# Revit family: Hager-Volta-IP30-Hollow_wall-empty-NoHosted-CH-en
name_source: partatom
category: Electrical Equipment
units: mm (PartAtom-declared; Revit-internal decimal feet)

## family parameters
Always vertical = Yes
Cut with Voids When Loaded = No
Panel Configuration = Two Columns, Circuits Across
Part Type = Panelboard
Room Calculation Point = No
Round Connector Dimension = Use Diameter
Shared = No
Work Plane-Based = Yes

## types (5) — shared parameters
Default Elevation = 1219 mm
EF000003 - Mounting method = EV000128 - Hollow wall
EF000007 - Colour = EV000202 - White
EF000008 - Width = 330 mm
EF000049 - Depth = 94 mm  [stored 0.308399 ft]
EF000116 - RAL-number = 9010
EF000118 - With mounting plate = No
EF000218 - Built-in depth = 90 mm  [stored 0.295276 ft]
EF000846 - Built-in width = 314 mm  [stored 1.03018 ft]
EF001062 - EMC-version = Yes
EF001088 - Extension possible = Yes
EF001131 - Internal depth = 92 mm
EF001134 - DIN-rail = No
EF001596 - Material housing = EV000139 - Plastic
EF002950 - Width in number of modular spacings = 12
EF006244 - Transparent cover/door = No
EF006306 - With lock = No
EF009212 - Cover model = EV000116 - Closed
EF015776 - Earthing terminal block = No
EF015777 - Neutral terminal block = No
EF015941 - Signal passing door = No
HG000002 - With door or cover = No
HG000003 - Range = Volta
HG000005 - Thickness = 3 mm  [stored 0.00984252 ft]
HG000006 - Flush mounted = Yes
HG000009 - Double swing door = No
HG000010 - Asymmetric doors = No
HG000011 - Empty rows from bottom = No
HG000017 - Distance between poles = 18 mm  [stored 0.0590551 ft]
Manufacturer = Hager
Type Comments = Volta
zero-valued in all types: HG000001 - Number of columns, HG000007 - Number of empty columns, HG000008 - Number of empty rows

## per-type parameters (varying)
| type | EF000040 - Height | EF000266 - Number of rows | EF000332 - Built-in height | HG000004 - Manufacturer reference | Model |
| Recessed mounted  W330 H355 D94.5 12 Modular spacings - VH12NK | 355 mm | 1 | 346 mm | VH12NK | VH12NK |
| Recessed mounted  W330 H484 D94.5 12 Modular spacings - VH24NK | 484 mm | 2 | 471 mm | VH24NK | VH24NK |
| Recessed mounted  W330 H609 D94.5 12 Modular spacings - VH36NK | 609 mm | 3 | 596 mm | VH36NK | VH36NK |
| Recessed mounted  W330 H734 D94.5 12 Modular spacings - VH48NK | 734 mm | 4 | 721 mm | VH48NK | VH48NK |
| Recessed mounted  W330 H880 D94.5 12 Modular spacings - VH60NK | 880 mm  [stored 2.88714 ft] | 5 | 846 mm  [stored 2.77559 ft] | VH60NK | VH60NK |

note: [stored X ft] marks values corroborated as IEEE doubles in the binary element streams (Revit-internal decimal feet)

## geometry (parser evidence)
native form markers: Sweep x14
no freeform markers — native parametric forms only
